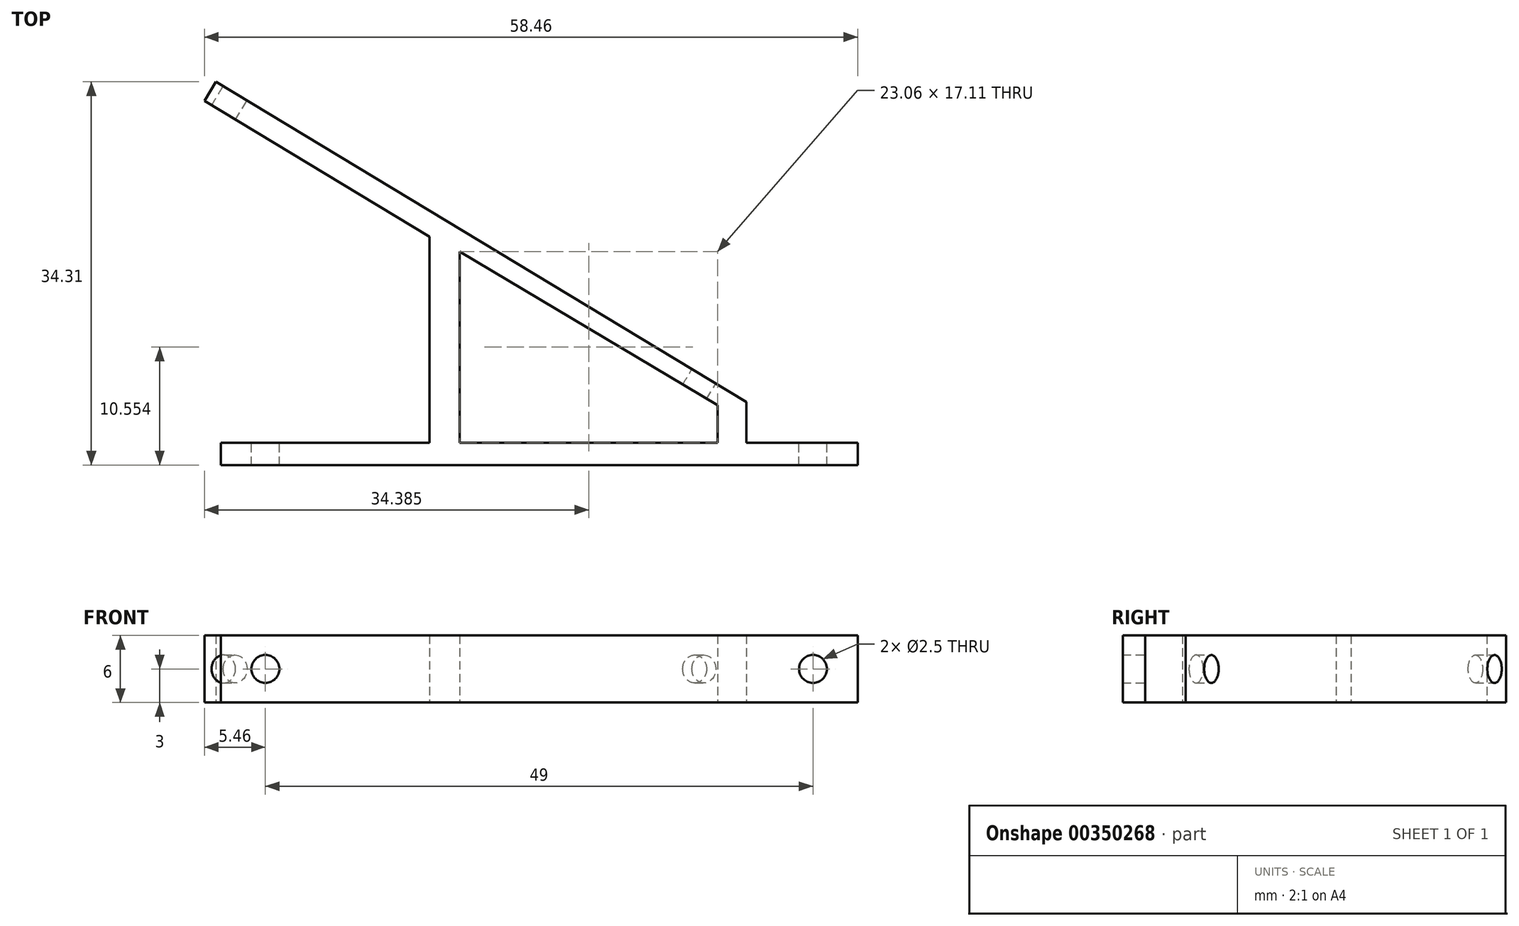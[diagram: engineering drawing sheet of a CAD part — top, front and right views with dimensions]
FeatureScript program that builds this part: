
annotation { "Feature Type Name" : "Feature", "Feature Type Description" : "" }
export const myFeature = defineFeature(function(context is Context, id is Id, definition is map)
    precondition{}
    {
        {
            var Q0;
            Q0=qCreatedBy(makeId("Top.planeOp"),FACE);
            var sketch = newSketch(context, id + "F0", { "sketchPlane" : qUnion([Q0])});
            skLineSegment(sketch, "E0.bottom", {"start": v(-57, 0) * mm, "end": v(-38.33, 0) * mm});
            skLineSegment(sketch, "E0.top", {"start": v(-57, -2) * mm, "end": v(0, -2) * mm});
            skLineSegment(sketch, "E0.left", {"start": v(-57, 0) * mm, "end": v(-57, -2) * mm});
            skLineSegment(sketch, "E0.right", {"start": v(0, 0) * mm, "end": v(0, -2) * mm});
            skLineSegment(sketch, "E1", {"start": v(-58.46, 30.6) * mm, "end": v(-57.42, 32.3) * mm});
            skLineSegment(sketch, "E2", {"start": v(-57.42, 32.3) * mm, "end": v(-9.96, 3.64) * mm});
            skLineSegment(sketch, "E3", {"start": v(-38.33, 0) * mm, "end": v(-38.33, 18.44) * mm});
            skLineSegment(sketch, "E4.trimOffspring", {"start": v(-38.33, 18.44) * mm, "end": v(-58.46, 30.6) * mm});
            skLineSegment(sketch, "E5.trimOffspring", {"start": v(-3.94, 0) * mm, "end": v(0, 0) * mm});
            skPoint(sketch, "E6.trimOffspring.start.orphan", {"position": v(-36.33, 0) * mm});
            skLineSegment(sketch, "E7", {"start": v(-35.6, 17.1) * mm, "end": v(-12.55, 3.35) * mm});
            skLineSegment(sketch, "E8", {"start": v(-6.92, 0) * mm, "end": v(-9.96, 0) * mm});
            skLineSegment(sketch, "E9", {"start": v(-35.6, 17.1) * mm, "end": v(-35.6, 0) * mm});
            skLineSegment(sketch, "E10", {"start": v(-9.96, 3.64) * mm, "end": v(-9.96, 0) * mm});
            skLineSegment(sketch, "E11", {"start": v(-12.55, 3.35) * mm, "end": v(-12.55, 0) * mm});
            skLineSegment(sketch, "E12", {"start": v(-9.96, 0) * mm, "end": v(0, 0) * mm});
            skLineSegment(sketch, "E13.trimOffspring", {"start": v(-12.55, 0) * mm, "end": v(-36.33, 0) * mm});
            skSolve(sketch);
        }
        {
            var Q0;
            Q0 = qSketchRegion(id + "F0", true);
            var Q1;
            Q1 = qSketchRegion(id + "F96PT0ErqWhOYXY_1", true);
            extrude(context, id + "F1", {"entities" : qUnion([Q0, Q1]), "endBound" : BoundingType.SYMMETRIC, "depth" : 6 * mm});
        }
        {
            var Q0;
            Q0=makeQuery(id+"F1.opExtrude","SWEPT_FACE",FACE,{"disambiguationData":[OSD([sQuery(id+"F0.wireOp",EDGE,"E0.top")])]});
            var sketch = newSketch(context, id + "F2", { "sketchPlane" : qUnion([Q0])});
            skCircle(sketch, "E14", {"center": v(-4, 0) * mm, "radius": 1.25 * mm});
            skCircle(sketch, "E15", {"center": v(-53, 0) * mm, "radius": 1.25 * mm});
            skSolve(sketch);
        }
        {
            var Q0;
            Q0=makeQuery(id+"F2.imprint","IMPRINT",FACE,{"disambiguationData":[TD([[makeQuery(id+"F2.imprint","IMPRINT",EDGE,{"derivedFrom":sQuery(id+"F2.wireOp",EDGE,"E15")}),1.0]])]});
            var Q1;
            Q1=makeQuery(id+"F2.imprint","IMPRINT",FACE,{"disambiguationData":[TD([[makeQuery(id+"F2.imprint","IMPRINT",EDGE,{"derivedFrom":sQuery(id+"F2.wireOp",EDGE,"E14")}),1.0]])]});
            extrude(context, id + "F3", {"entities" : qUnion([Q0, Q1]), "operationType" : NewBodyOperationType.REMOVE, "endBound" : BoundingType.SYMMETRIC, "depth" : 25 * mm});
        }
        {
            var Q0;
            Q0=makeQuery(id+"F1.opExtrude","SWEPT_FACE",FACE,{"disambiguationData":[OSD([sQuery(id+"F0.wireOp",EDGE,"E2")])]});
            var sketch = newSketch(context, id + "F4", { "sketchPlane" : qUnion([Q0])});
            skCircle(sketch, "E16", {"center": v(63.85, 0) * mm, "radius": 1.25 * mm});
            skCircle(sketch, "E17", {"center": v(14.85, 0) * mm, "radius": 1.25 * mm});
            skSolve(sketch);
        }
        {
            var Q0;
            Q0 = qSketchRegion(id + "F4", true);
            extrude(context, id + "F5", {"entities" : qUnion([Q0]), "operationType" : NewBodyOperationType.REMOVE, "oppositeDirection" : true, "depth" : 4 * mm});
        }
    });
